# Revit family: GSY27
name_source: partatom
category: Structural Framing
revit_build: Autodesk Revit 2018 (Build: 20190510_1515(x64)
units: mm (PartAtom-declared; Revit-internal decimal feet)

## family parameters
Always export as geometry = No
Always vertical = Yes
Cut with Voids When Loaded = No
Material for Model Behavior = Other
OmniClass Number = 23.25.30.11.14.14
OmniClass Title = Beams
Section Shape = Not Defined
Shared = No
Show family pre-cut in plan views = Yes

## types (5) — shared parameters
Manufacturer = Give Steel A/S
d = 15 mm  [stored 0.0492126 ft]
hw = 230 mm  [stored 0.754593 ft]
t1 = 40 mm  [stored 0.131234 ft]
t2 = 25 mm  [stored 0.082021 ft]

## per-type parameters (varying)
| type | b1 | b2 |
| GSY27/15-40 | 150 mm  [stored 0.492126 ft] | 400 mm  [stored 1.31234 ft] |
| GSY27/18-43 | 180 mm  [stored 0.590551 ft] | 430 mm |
| GSY27/22-47 | 220 mm  [stored 0.721785 ft] | 470 mm  [stored 1.54199 ft] |
| GSY27/27-52 | 270 mm  [stored 0.885827 ft] | 520 mm  [stored 1.70604 ft] |
| GSY27/30-55 | 300 mm | 550 mm |

note: [stored X ft] marks values corroborated as IEEE doubles in the binary element streams (Revit-internal decimal feet)

## geometry (parser evidence)
native form markers: Sweep x3
no freeform markers — native parametric forms only
